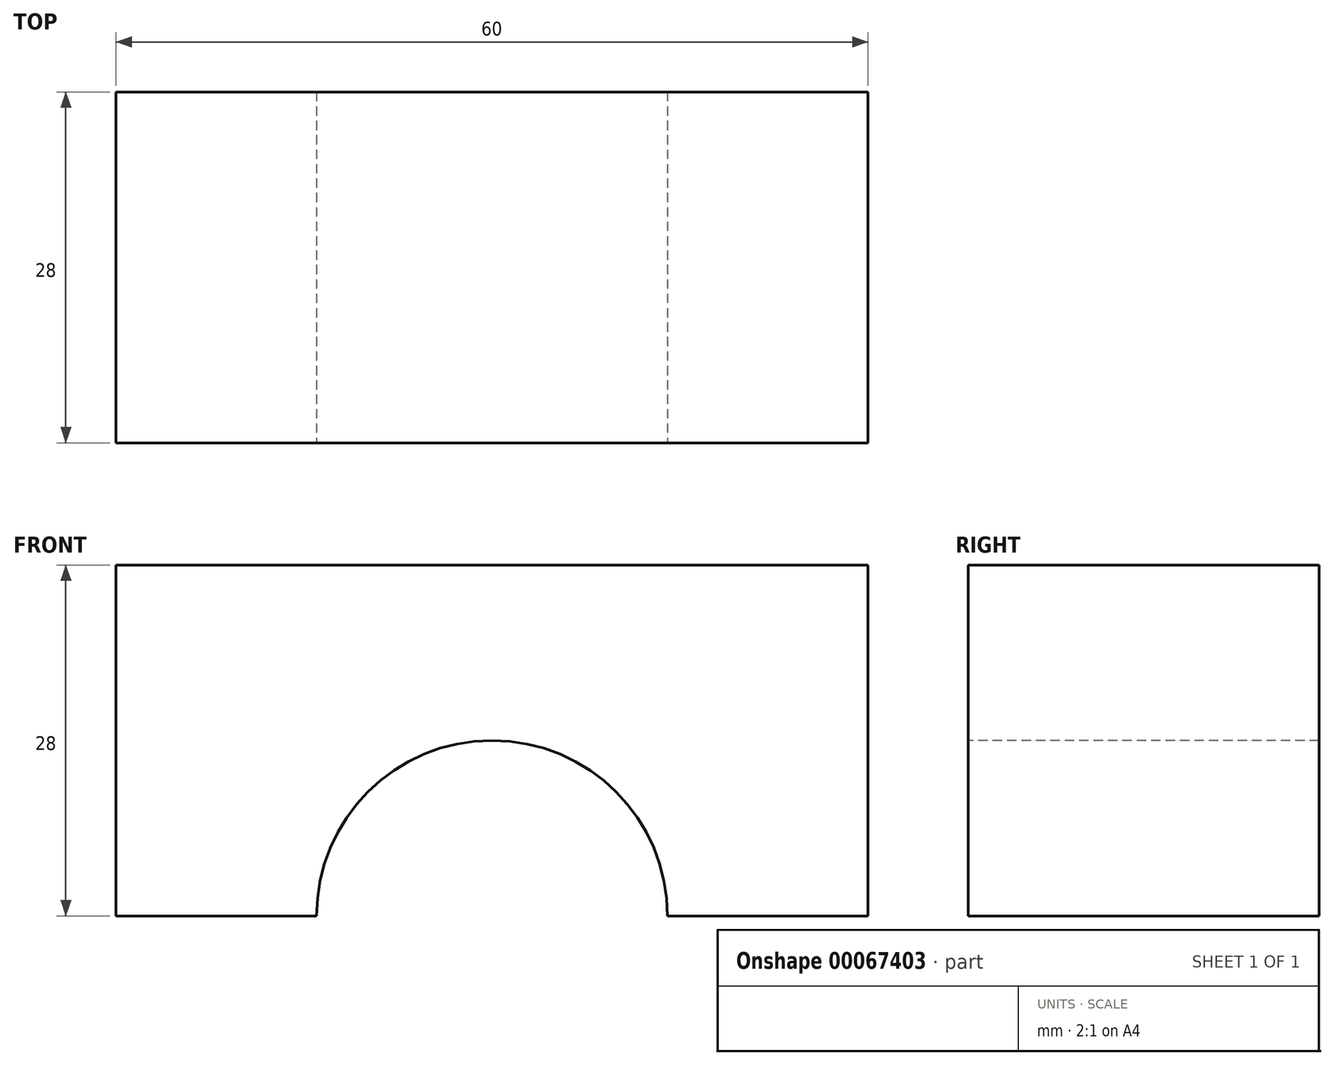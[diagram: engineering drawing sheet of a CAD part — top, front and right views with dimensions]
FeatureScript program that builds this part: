
annotation { "Feature Type Name" : "Feature", "Feature Type Description" : "" }
export const myFeature = defineFeature(function(context is Context, id is Id, definition is map)
    precondition{}
    {
        {
            var Q0;
            Q0=qCreatedBy(makeId("Top.planeOp"),FACE);
            var sketch = newSketch(context, id + "F0", { "sketchPlane" : qUnion([Q0])});
            skLineSegment(sketch, "E0.bottom", {"start": v(30, -14) * mm, "end": v(-30, -14) * mm});
            skLineSegment(sketch, "E0.top", {"start": v(30, 14) * mm, "end": v(-30, 14) * mm});
            skLineSegment(sketch, "E0.left", {"start": v(30, -14) * mm, "end": v(30, 14) * mm});
            skLineSegment(sketch, "E0.right", {"start": v(-30, -14) * mm, "end": v(-30, 14) * mm});
            skPoint(sketch, "E0.middle", {"position": v(0, 0) * mm});
            skSolve(sketch);
        }
        {
            var Q0;
            Q0 = qSketchRegion(id + "F0", true);
            extrude(context, id + "F1", {"entities" : qUnion([Q0]), "endBound" : BoundingType.SYMMETRIC, "depth" : 28 * mm});
        }
        {
            var Q0;
            Q0=qCreatedBy(makeId("Front.planeOp"),FACE);
            var sketch = newSketch(context, id + "F2", { "sketchPlane" : qUnion([Q0])});
            skCircle(sketch, "E1", {"center": v(0, -14) * mm, "radius": 14 * mm});
            skSolve(sketch);
        }
        {
            var Q0;
            Q0=makeQuery(id+"F2.imprint","IMPRINT",FACE,{"disambiguationData":[TD([[makeQuery(id+"F2.imprint","IMPRINT",EDGE,{"derivedFrom":sQuery(id+"F2.wireOp",EDGE,"E1")}),1.0]])]});
            var Q1;
            Q1=sQuery(id+"F2.wireOp",EDGE,"E1");
            extrude(context, id + "F3", {"entities" : qUnion([Q0]), "operationType" : NewBodyOperationType.REMOVE, "surfaceEntities" : qUnion([Q1]), "endBound" : BoundingType.SYMMETRIC, "oppositeDirection" : true, "depth" : 100 * mm});
        }
    });
